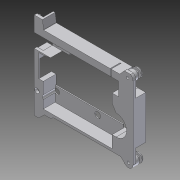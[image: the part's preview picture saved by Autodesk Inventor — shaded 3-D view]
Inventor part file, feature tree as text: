
AUTODESK INVENTOR PART (.ipt)
format: ipt  version: 2011 (Build 150239000, 239)  size: 231,936 bytes
history: native  units: in
note: dims shown in document units (in); Inventor stores cm internally (conversion verified against a paired STEP export)
features: extrude x2, sketch x2, other x1, imported_body x1
ambient origin geometry x8: Origin, YZ Plane, XZ Plane, XY Plane, X Axis, Y Axis, Z Axis, Center Point
feature tree (6):
  other  "MotorTray"
  imported_body  "Base1"
  extrude  "Extrusion1"  Depth=0.3937in TaperAngle=0.0deg
  extrude  "Extrusion2"  [1 undecoded]
  sketch  "Sketch1"  dims[d0=0.0in d1=0.0in d2=0.3937in d3=0.0in]
  sketch  "Sketch2"
note: 1 required parameter value undecoded (feature->parameter linkage not recoverable at this tier; creation-order binding heuristic only, values carry confidence <= 0.55)
